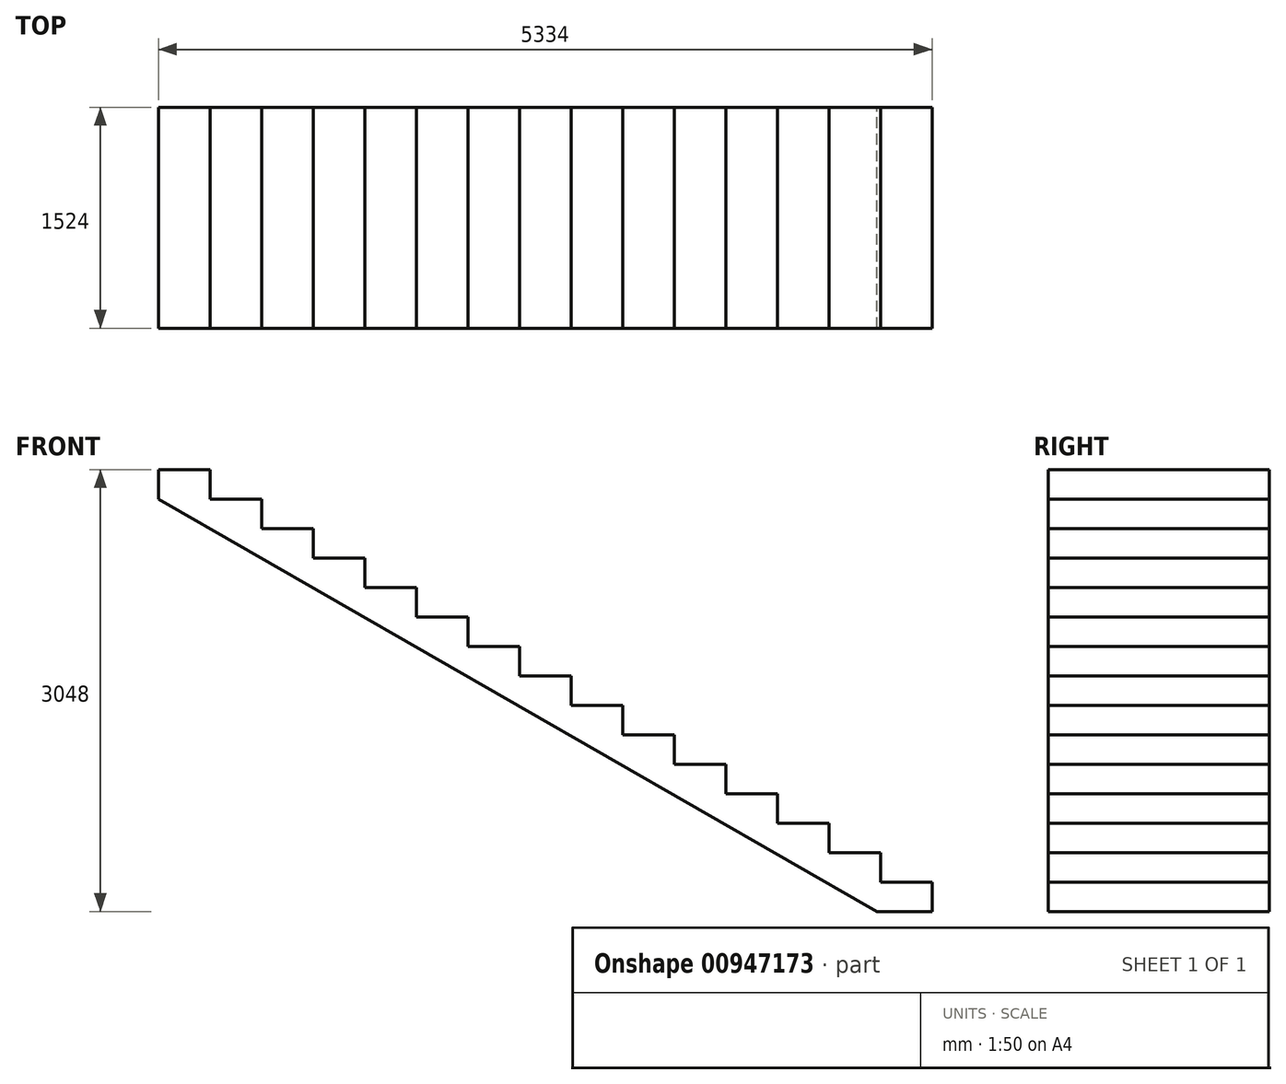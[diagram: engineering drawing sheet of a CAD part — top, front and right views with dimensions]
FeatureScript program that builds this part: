
annotation { "Feature Type Name" : "Feature", "Feature Type Description" : "" }
export const myFeature = defineFeature(function(context is Context, id is Id, definition is map)
    precondition{}
    {
        {
            var Q0;
            Q0=qCreatedBy(makeId("Front.planeOp"),FACE);
            var sketch = newSketch(context, id + "F0", { "sketchPlane" : qUnion([Q0])});
            skLineSegment(sketch, "E0", {"start": v(0, 0) * mm, "end": v(0, 203.2) * mm});
            skLineSegment(sketch, "E1", {"start": v(0, 203.2) * mm, "end": v(-355.6, 203.2) * mm});
            skLineSegment(sketch, "E2", {"start": v(-355.6, 203.2) * mm, "end": v(-355.6, 406.4) * mm});
            skLineSegment(sketch, "E3", {"start": v(-355.6, 406.4) * mm, "end": v(-711.2, 406.4) * mm});
            skLineSegment(sketch, "E4", {"start": v(-711.2, 406.4) * mm, "end": v(-711.2, 609.6) * mm});
            skLineSegment(sketch, "E5", {"start": v(-711.2, 609.6) * mm, "end": v(-1066.8, 609.6) * mm});
            skLineSegment(sketch, "E6", {"start": v(-1066.8, 609.6) * mm, "end": v(-1066.8, 812.8) * mm});
            skLineSegment(sketch, "E7", {"start": v(-1066.8, 812.8) * mm, "end": v(-1422.4, 812.8) * mm});
            skLineSegment(sketch, "E8", {"start": v(-1422.4, 812.8) * mm, "end": v(-1422.4, 1016) * mm});
            skLineSegment(sketch, "E9", {"start": v(-1422.4, 1016) * mm, "end": v(-1778, 1016) * mm});
            skLineSegment(sketch, "E10", {"start": v(-1778, 1016) * mm, "end": v(-1778, 1219.2) * mm});
            skLineSegment(sketch, "E11", {"start": v(-1778, 1219.2) * mm, "end": v(-2133.6, 1219.2) * mm});
            skLineSegment(sketch, "E12", {"start": v(-2133.6, 1219.2) * mm, "end": v(-2133.6, 1422.4) * mm});
            skLineSegment(sketch, "E13", {"start": v(-2133.6, 1422.4) * mm, "end": v(-2489.2, 1422.4) * mm});
            skLineSegment(sketch, "E14", {"start": v(0, 0) * mm, "end": v(-381, 0) * mm});
            skLineSegment(sketch, "E15", {"start": v(-2489.2, 1422.4) * mm, "end": v(-2489.2, 1625.6) * mm});
            skLineSegment(sketch, "E16", {"start": v(-2489.2, 1625.6) * mm, "end": v(-2844.8, 1625.6) * mm});
            skLineSegment(sketch, "E17", {"start": v(-2844.8, 1625.6) * mm, "end": v(-2844.8, 1828.8) * mm});
            skLineSegment(sketch, "E18", {"start": v(-2844.8, 1828.8) * mm, "end": v(-3200.4, 1828.8) * mm});
            skLineSegment(sketch, "E19", {"start": v(-3200.4, 1828.8) * mm, "end": v(-3200.4, 2032) * mm});
            skLineSegment(sketch, "E20", {"start": v(-3200.4, 2032) * mm, "end": v(-3556, 2032) * mm});
            skLineSegment(sketch, "E21", {"start": v(-3556, 2032) * mm, "end": v(-3556, 2235.2) * mm});
            skLineSegment(sketch, "E22", {"start": v(-3556, 2235.2) * mm, "end": v(-3911.6, 2235.2) * mm});
            skLineSegment(sketch, "E23", {"start": v(-3911.6, 2235.2) * mm, "end": v(-3911.6, 2438.4) * mm});
            skLineSegment(sketch, "E24", {"start": v(-3911.6, 2438.4) * mm, "end": v(-4267.2, 2438.4) * mm});
            skLineSegment(sketch, "E25", {"start": v(-4267.2, 2438.4) * mm, "end": v(-4267.2, 2641.6) * mm});
            skLineSegment(sketch, "E26", {"start": v(-4267.2, 2641.6) * mm, "end": v(-4622.8, 2641.6) * mm});
            skLineSegment(sketch, "E27", {"start": v(-4622.8, 2641.6) * mm, "end": v(-4622.8, 2844.8) * mm});
            skLineSegment(sketch, "E28", {"start": v(-4622.8, 2844.8) * mm, "end": v(-4978.4, 2844.8) * mm});
            skLineSegment(sketch, "E29", {"start": v(-381, 0) * mm, "end": v(-5334, 2844.8) * mm});
            skLineSegment(sketch, "E30", {"start": v(-8178.8, 0) * mm, "end": v(0, 0) * mm, "construction": true});
            skLineSegment(sketch, "E31", {"start": v(-4978.4, 2844.8) * mm, "end": v(-4978.4, 0) * mm, "construction": true});
            skLineSegment(sketch, "E32", {"start": v(-4978.4, 2844.8) * mm, "end": v(-4978.4, 3048) * mm});
            skLineSegment(sketch, "E33", {"start": v(-4978.4, 3048) * mm, "end": v(-5334, 3048) * mm});
            skLineSegment(sketch, "E34", {"start": v(-5334, 3048) * mm, "end": v(-5334, 2844.8) * mm});
            skLineSegment(sketch, "E35", {"start": v(-5334, 3048) * mm, "end": v(-5334, 0) * mm, "construction": true});
            skSolve(sketch);
        }
        {
            var Q0;
            Q0 = qSketchRegion(id + "F0", true);
            extrude(context, id + "F1", {"entities" : qUnion([Q0]), "depth" : 1524 * mm, "offsetDistance" : 25.4 * mm});
        }
    });
